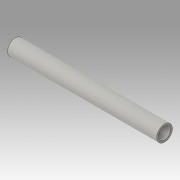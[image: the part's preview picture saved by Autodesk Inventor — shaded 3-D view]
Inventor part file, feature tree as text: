
AUTODESK INVENTOR PART (.ipt)
format: ipt  version: 2016 (Build 200138000, 138)  size: 77,312 bytes
history: native  units: in
note: dims shown in document units (in); Inventor stores cm internally (conversion verified against a paired STEP export)
features: extrude x1, sketch x1
ambient origin geometry x8: Origin, YZ Plane, XZ Plane, XY Plane, X Axis, Y Axis, Z Axis, Center Point
bodies: Solid1 (feature_tree)
feature tree (2):
  extrude  "Extrusion1"  Depth=6.0in
  sketch  "Sketch1"  dims[d0=0.635in d1=0.48in d2=6.0in d3=0.0in]
